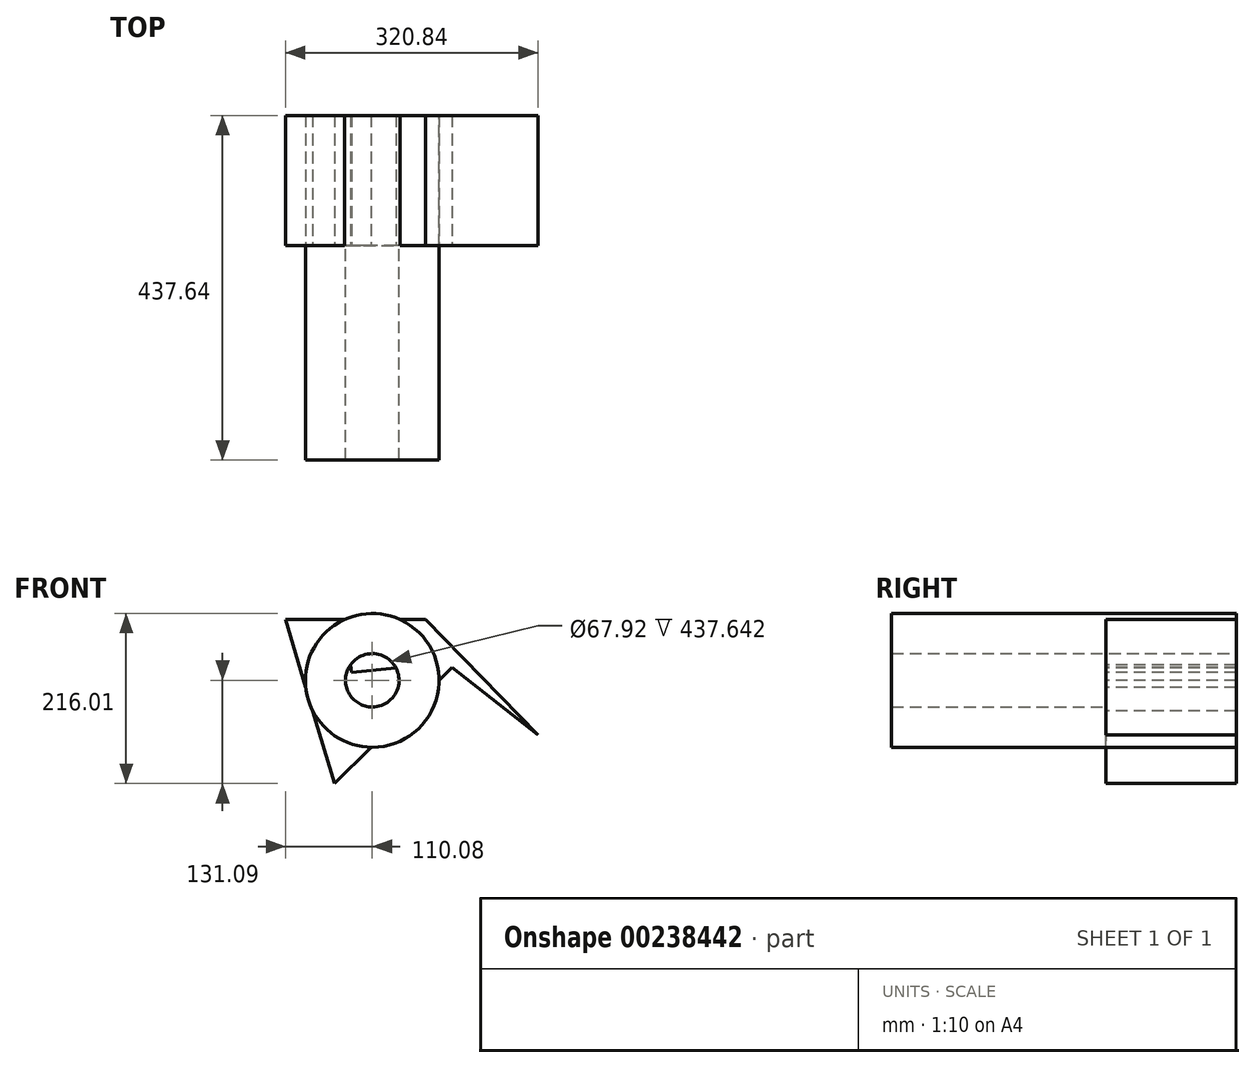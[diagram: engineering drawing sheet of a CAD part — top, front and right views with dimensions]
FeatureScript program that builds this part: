
annotation { "Feature Type Name" : "Feature", "Feature Type Description" : "" }
export const myFeature = defineFeature(function(context is Context, id is Id, definition is map)
    precondition{}
    {
        {
            var Q0;
            Q0=qCreatedBy(makeId("Front.planeOp"),FACE);
            var sketch = newSketch(context, id + "F0", { "sketchPlane" : qUnion([Q0])});
            skCircle(sketch, "E0", {"center": v(0, 0) * mm, "radius": 84.92 * mm});
            skCircle(sketch, "E1", {"center": v(0, 0) * mm, "radius": 33.96 * mm});
            skSolve(sketch);
        }
        {
            var Q0;
            Q0 = qSketchRegion(id + "F0", true);
            extrude(context, id + "F1", {"entities" : qUnion([Q0]), "depth" : 272.3 * mm});
        }
        {
            var Q0;
            Q0=qCreatedBy(makeId("Front.planeOp"),FACE);
            var sketch = newSketch(context, id + "F2", { "sketchPlane" : qUnion([Q0])});
            skLineSegment(sketch, "E2", {"start": v(101.2, 16.22) * mm, "end": v(-48.13, -131.09) * mm});
            skLineSegment(sketch, "E3", {"start": v(-48.13, -131.09) * mm, "end": v(-110.08, 77.21) * mm});
            skLineSegment(sketch, "E4", {"start": v(-110.08, 77.21) * mm, "end": v(67.95, 77.21) * mm});
            skLineSegment(sketch, "E5", {"start": v(67.95, 77.21) * mm, "end": v(210.76, -69.53) * mm});
            skLineSegment(sketch, "E6", {"start": v(210.76, -69.53) * mm, "end": v(101.2, 16.22) * mm});
            skLineSegment(sketch, "E7", {"start": v(31.43, 16.22) * mm, "end": v(-26.6, 10.08) * mm});
            skLineSegment(sketch, "E8", {"start": v(-26.6, 10.08) * mm, "end": v(-30.76, 49.26) * mm});
            skLineSegment(sketch, "E9", {"start": v(-30.76, 49.26) * mm, "end": v(30.74, 55.77) * mm});
            skLineSegment(sketch, "E10", {"start": v(30.74, 55.77) * mm, "end": v(31.43, 16.22) * mm});
            skSolve(sketch);
        }
        {
            var Q0;
            Q0=makeQuery(id+"F2.imprint","IMPRINT",FACE,{"disambiguationData":[TD([[makeQuery(id+"F2.imprint","IMPRINT",EDGE,{"derivedFrom":sQuery(id+"F2.wireOp",EDGE,"E2")}),-1.0]])]});
            var Q1;
            Q1=makeQuery(id+"F1.opExtrude","CAP_FACE",FACE,{"disambiguationData":[OSD([sQuery(id+"F0.wireOp",EDGE,"E0"),sQuery(id+"F0.wireOp",EDGE,"E1")])],"isStart":true});
            extrude(context, id + "F3", {"entities" : qUnion([Q0, Q1]), "operationType" : NewBodyOperationType.ADD, "oppositeDirection" : true, "depth" : 165.35 * mm});
        }
    });
